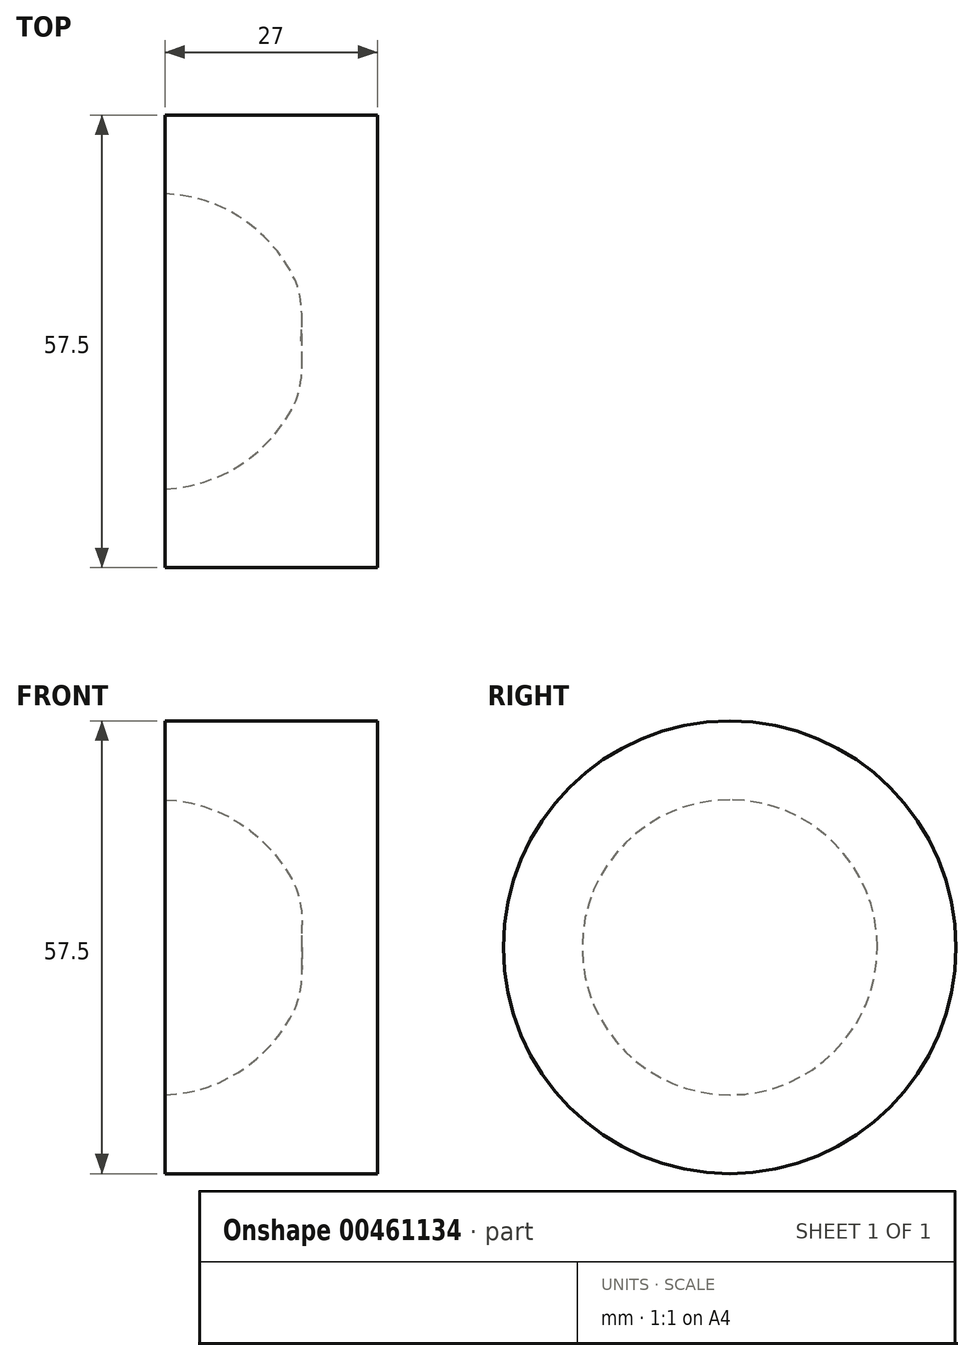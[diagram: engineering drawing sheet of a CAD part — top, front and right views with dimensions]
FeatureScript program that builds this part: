
annotation { "Feature Type Name" : "Feature", "Feature Type Description" : "" }
export const myFeature = defineFeature(function(context is Context, id is Id, definition is map)
    precondition{}
    {
        {
            var Q0;
            Q0=qCreatedBy(makeId("Top.planeOp"),FACE);
            var sketch = newSketch(context, id + "F0", { "sketchPlane" : qUnion([Q0])});
            skLineSegment(sketch, "E0", {"start": v(17.3, 0) * mm, "end": v(27, 0) * mm});
            skLineSegment(sketch, "E1", {"start": v(0, 18.75) * mm, "end": v(0, 28.75) * mm});
            skLineSegment(sketch, "E2", {"start": v(0, 28.75) * mm, "end": v(27, 28.75) * mm});
            skLineSegment(sketch, "E3", {"start": v(27, 28.75) * mm, "end": v(27, 0) * mm});
            skFitSpline(sketch, "E4", {"points": [v(17.3, 0) * mm, v(15.84, 9.13) * mm, v(0, 18.75) * mm], "startDerivative": vector(1.95, 30.18) * mm, "endDerivative": vector(-42.58, 1.7) * mm});
            skSolve(sketch);
        }
        {
            var Q0;
            Q0=makeQuery(id+"F0.imprint","IMPRINT",FACE,{"disambiguationData":[TD([[makeQuery(id+"F0.imprint","IMPRINT",EDGE,{"derivedFrom":sQuery(id+"F0.wireOp",EDGE,"E0")}),1.0]])]});
            var Q1;
            Q1=sQuery(id+"F0.wireOp",EDGE,"E0");
            revolve(context, id + "F1", {"entities" : qUnion([Q0]), "axis" : qUnion([Q1]), "revolveType" : RevolveType.FULL});
        }
    });
